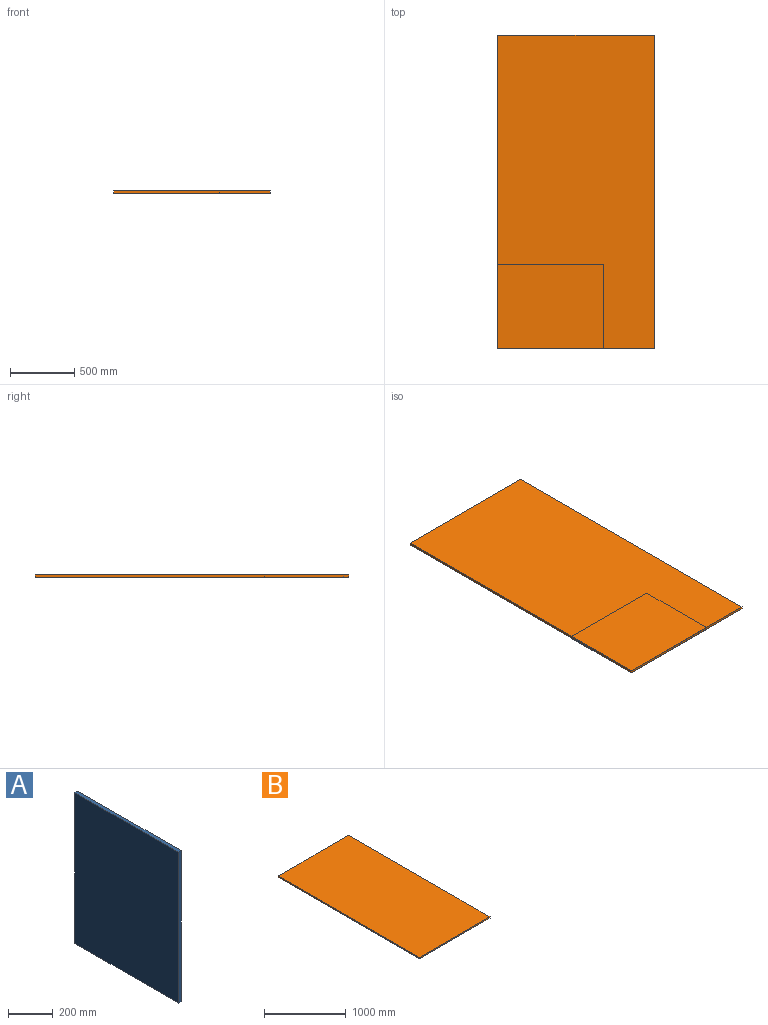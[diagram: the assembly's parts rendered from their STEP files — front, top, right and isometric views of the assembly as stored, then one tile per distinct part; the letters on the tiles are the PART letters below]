
ASSEMBLY  parts=2 mates=1
PART A: 6 faces, bbox 18.3x655.6x827.1 mm
  f0: plane 827.09x18.26mm, normal (0,1,0), area 15099.5mm2, adj f1,f3,f4,f5
  f1: plane 827.09x655.64mm, normal (-1,0,0), area 542269.6mm2, adj f0,f2,f4,f5
  f2: plane 827.09x18.26mm, normal (0,-1,0), area 15099.5mm2, adj f1,f3,f4,f5
  f3: plane 827.09x655.64mm, normal (1,0,0), area 542269.6mm2, adj f0,f2,f4,f5
  f4: plane 655.64x18.26mm, normal (0,0,-1), area 11969.5mm2, adj f0,f1,f2,f3
  f5: plane 655.64x18.26mm, normal (0,0,1), area 11969.5mm2, adj f0,f1,f2,f3
PART B: 6 faces, bbox 1219.2x2438.4x18.3 mm
  f0: plane 2438.4x18.26mm, normal (1,0,0), area 44516mm2, adj f1,f3,f4,f5
  f1: plane 1219.2x18.26mm, normal (0,1,0), area 22258mm2, adj f0,f2,f4,f5
  f2: plane 2438.4x18.26mm, normal (-1,0,0), area 44516mm2, adj f1,f3,f4,f5
  f3: plane 1219.2x18.26mm, normal (0,-1,0), area 22258mm2, adj f0,f2,f4,f5
  f4: plane 2438.4x1219.2mm, normal (0,0,1), area 2972897.3mm2, adj f0,f1,f2,f3
  f5: plane 2438.4x1219.2mm, normal (0,0,-1), area 2972897.3mm2, adj f0,f1,f2,f3
PLACE A rot(axis=(0,1,0),90deg) t=(-11.91,327.82,-711.2)mm
PLACE B t=(1219.2,0,0)mm
MATE fastened A.f3 <-> B.f5  axis (0,0,-1) through (0,0,0)mm
